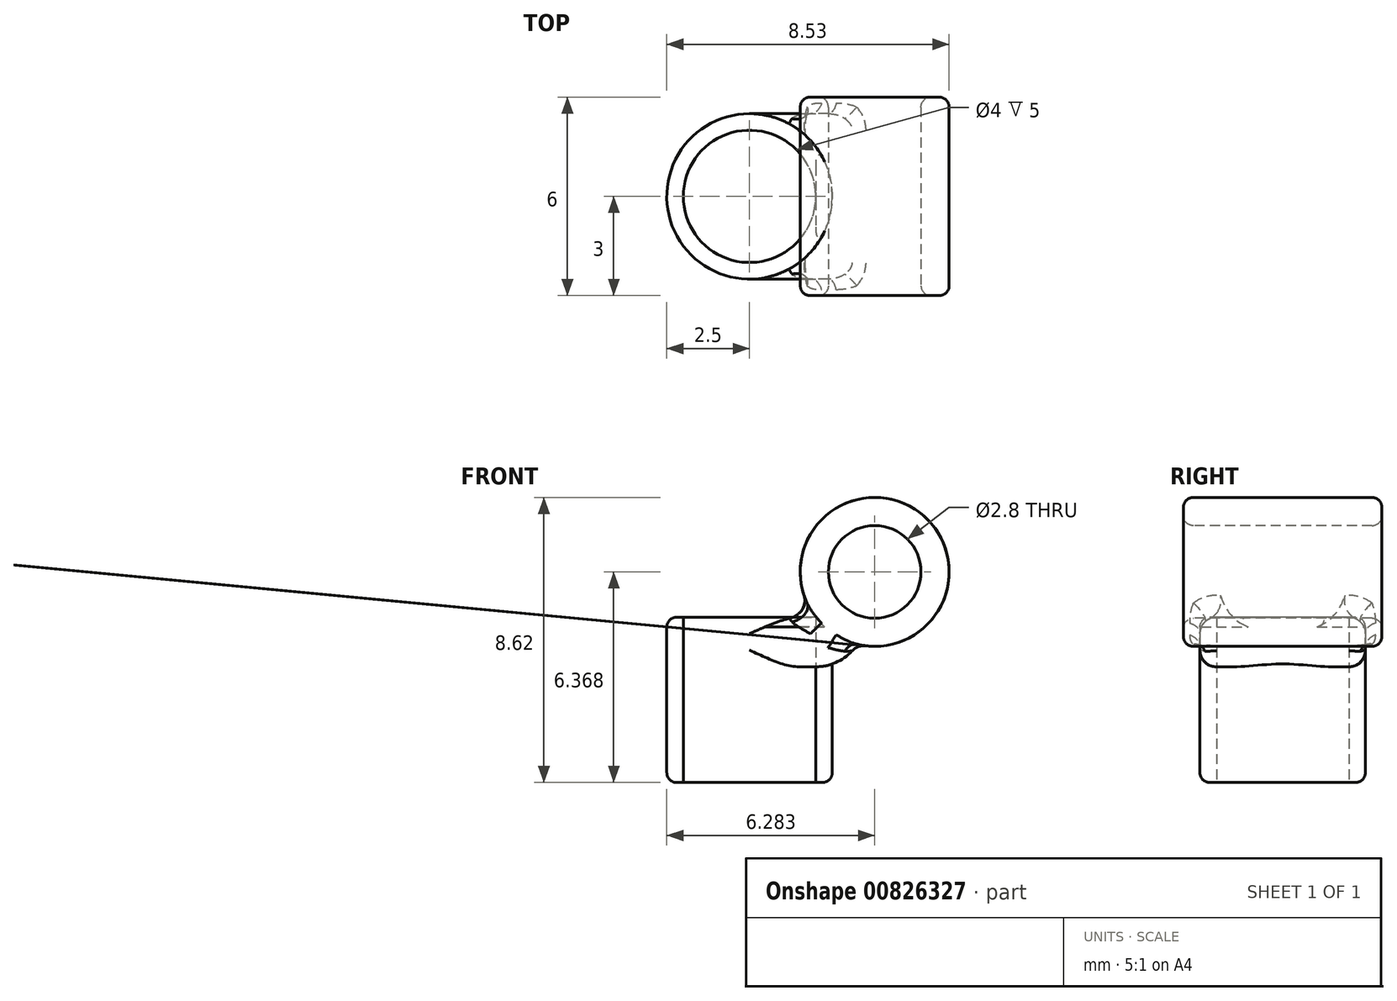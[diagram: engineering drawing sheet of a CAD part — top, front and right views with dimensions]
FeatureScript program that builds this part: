
annotation { "Feature Type Name" : "Feature", "Feature Type Description" : "" }
export const myFeature = defineFeature(function(context is Context, id is Id, definition is map)
    precondition{}
    {
        {
            var Q0;
            Q0=qCreatedBy(makeId("Top.planeOp"),FACE);
            var sketch = newSketch(context, id + "F0", { "sketchPlane" : qUnion([Q0])});
            skCircle(sketch, "E0", {"center": v(0, 0) * mm, "radius": 2 * mm});
            skCircle(sketch, "E1", {"center": v(0, 0) * mm, "radius": 2.5 * mm});
            skSolve(sketch);
        }
        {
            var Q0;
            Q0 = qSketchRegion(id + "F0", true);
            extrude(context, id + "F1", {"entities" : qUnion([Q0]), "depth" : 5 * mm, "offsetDistance" : 25 * mm});
        }
        {
            var Q0;
            Q0=qCreatedBy(makeId("Front.planeOp"),FACE);
            cPlane(context, id + "F2", {"entities" : qUnion([Q0]), "cplaneType" : CPlaneType.OFFSET, "offset" : 3 * mm, "width" : 150 * mm, "height" : 150 * mm});
        }
        {
            var Q0;
            Q0=qCreatedBy(id+"F2.planeOp",FACE);
            var sketch = newSketch(context, id + "F3", { "sketchPlane" : qUnion([Q0])});
            skCircle(sketch, "E2", {"center": v(3.78, 6.37) * mm, "radius": 2.25 * mm});
            skPoint(sketch, "E3.start.orphan", {"position": v(5, 0) * mm});
            skCircle(sketch, "E4", {"center": v(3.78, 6.37) * mm, "radius": 1.4 * mm});
            skSolve(sketch);
        }
        {
            var Q0;
            Q0 = qSketchRegion(id + "F3", true);
            extrude(context, id + "F4", {"entities" : qUnion([Q0]), "oppositeDirection" : true, "depth" : 6 * mm, "offsetDistance" : 25 * mm});
        }
        {
            var Q0;
            Q0=qCreatedBy(makeId("Top.planeOp"),FACE);
            cPlane(context, id + "F5", {"entities" : qUnion([Q0]), "cplaneType" : CPlaneType.OFFSET, "offset" : 3.5 * mm, "width" : 150 * mm, "height" : 150 * mm});
        }
        {
            var Q0;
            Q0=qCreatedBy(id+"F5.planeOp",FACE);
            var sketch = newSketch(context, id + "F6", { "sketchPlane" : qUnion([Q0])});
            skArc(sketch, "E5.0", {"start": v(0, -2.5) * mm, "mid": v(2.5, 0) * mm, "end": v(0, 2.5) * mm});
            skLineSegment(sketch, "E6", {"start": v(0, 2.5) * mm, "end": v(3.5, 2.5) * mm});
            skLineSegment(sketch, "E7", {"start": v(0, -2.5) * mm, "end": v(3.5, -2.5) * mm});
            skLineSegment(sketch, "E8", {"start": v(3.5, -2.5) * mm, "end": v(3.5, 2.5) * mm});
            skPoint(sketch, "E9.start.orphan", {"position": v(0, -0.17) * mm});
            skPoint(sketch, "E10.bottom.start.orphan", {"position": v(0, 78.67) * mm});
            skSolve(sketch);
        }
        {
            var Q0;
            Q0 = qSketchRegion(id + "F6", true);
            extrude(context, id + "F7", {"entities" : qUnion([Q0]), "depth" : 1.5 * mm, "offsetDistance" : 25 * mm});
        }
        {
            var Q0;
            Q0=makeQuery(id+"F7.opExtrude","CAP_EDGE",EDGE,{"disambiguationData":[OSD([sQuery(id+"F6.wireOp",EDGE,"E8")])],"isStart":true});
            fillet(context, id + "F8", {"entities" : qUnion([Q0]), "radius" : 1.5 * mm, "tangentPropagation" : true, "allowEdgeOverflow" : false});
        }
        {
            var Q0;
            Q0=makeQuery(id+"F7.opExtrude","CAP_EDGE",EDGE,{"disambiguationData":[OSD([sQuery(id+"F6.wireOp",EDGE,"E7")])],"isStart":true});
            var Q1;
            Q1=makeQuery(id+"F7.opExtrude","CAP_EDGE",EDGE,{"disambiguationData":[OSD([sQuery(id+"F6.wireOp",EDGE,"E7")])],"isStart":false});
            var Q2;
            Q2=makeQuery(id+"F7.opExtrude","CAP_EDGE",EDGE,{"disambiguationData":[OSD([sQuery(id+"F6.wireOp",EDGE,"E6")])],"isStart":true});
            var Q3;
            Q3=makeQuery(id+"F7.opExtrude","CAP_EDGE",EDGE,{"disambiguationData":[OSD([sQuery(id+"F6.wireOp",EDGE,"E6")])],"isStart":false});
            var Q4;
            {var subQ0=sQuery(id+"F6.wireOp",EDGE,"E8");Q4=makeQuery(id+"F8.opFillet","BLEND_EDGE",EDGE,{"blendedFrom":[makeQuery(id+"F7.opExtrude","CAP_EDGE",EDGE,{"disambiguationData":[OSD([subQ0])],"isStart":true}),makeQuery(id+"F7.opExtrude","CAP_FACE",FACE,{"disambiguationData":[OSD([sQuery(id+"F6.wireOp",EDGE,"E5.0"),sQuery(id+"F6.wireOp",EDGE,"E6"),sQuery(id+"F6.wireOp",EDGE,"E7"),subQ0])],"isStart":false})],"blendedInto":[makeQuery(id+"F7.opExtrude","CAP_FACE",FACE,{"disambiguationData":[OSD([sQuery(id+"F6.wireOp",EDGE,"E5.0"),sQuery(id+"F6.wireOp",EDGE,"E6"),sQuery(id+"F6.wireOp",EDGE,"E7"),subQ0])],"isStart":false})]});}
            fillet(context, id + "F9", {"entities" : qUnion([Q0, Q1, Q2, Q3, Q4]), "radius" : 0.5 * mm, "tangentPropagation" : true, "allowEdgeOverflow" : false});
        }
        {
            var Q0;
            Q0=makeQuery(id+"F4.opExtrude","CAP_FACE",FACE,{"disambiguationData":[OSD([sQuery(id+"F3.wireOp",EDGE,"E2"),sQuery(id+"F3.wireOp",EDGE,"E4")])],"isStart":true});
            var Q1;
            Q1=makeQuery(id+"F4.opExtrude","CAP_EDGE",EDGE,{"disambiguationData":[OSD([sQuery(id+"F3.wireOp",EDGE,"E4")])],"isStart":false});
            var Q2;
            Q2=makeQuery(id+"F4.opExtrude","CAP_FACE",FACE,{"disambiguationData":[OSD([sQuery(id+"F3.wireOp",EDGE,"E2"),sQuery(id+"F3.wireOp",EDGE,"E4")])],"isStart":false});
            var Q3;
            Q3=makeQuery(id+"F1.opExtrude","CAP_EDGE",EDGE,{"disambiguationData":[OSD([sQuery(id+"F0.wireOp",EDGE,"E1")])],"isStart":false});
            var Q4;
            Q4=makeQuery(id+"F1.opExtrude","CAP_EDGE",EDGE,{"disambiguationData":[OSD([sQuery(id+"F0.wireOp",EDGE,"E1")])],"isStart":true});
            fillet(context, id + "F10", {"entities" : qUnion([Q0, Q1, Q2, Q3, Q4]), "radius" : 0.3 * mm, "tangentPropagation" : true, "allowEdgeOverflow" : false});
        }
        {
            var Q0;
            Q0=makeQuery(id+"F1.opExtrude","SWEPT_BODY",BODY,{"disambiguationData":[OSD([sQuery(id+"F0.wireOp",EDGE,"E0"),sQuery(id+"F0.wireOp",EDGE,"E1")])]});
            var Q1;
            Q1=makeQuery(id+"F4.opExtrude","SWEPT_BODY",BODY,{"disambiguationData":[OSD([sQuery(id+"F3.wireOp",EDGE,"E2"),sQuery(id+"F3.wireOp",EDGE,"E4")])]});
            var Q2;
            Q2=makeQuery(id+"F7.opExtrude","SWEPT_BODY",BODY,{"disambiguationData":[OSD([sQuery(id+"F6.wireOp",EDGE,"E5.0"),sQuery(id+"F6.wireOp",EDGE,"E6"),sQuery(id+"F6.wireOp",EDGE,"E7"),sQuery(id+"F6.wireOp",EDGE,"E8")])]});
            booleanBodies(context, id + "F11", {"operationType" : BooleanOperationType.UNION, "tools" : qUnion([Q0, Q1, Q2])});
        }
        {
            var Q0;
            Q0=makeQuery(id+"F11.opBoolean","INTERSECT",EDGE,{"derivedFrom":[makeQuery(id+"F8.opFillet","BLEND_FACE",FACE,{"disambiguationData":[OSD([sQuery(id+"F6.wireOp",EDGE,"E8")])]}),makeQuery(id+"F4.opExtrude","SWEPT_FACE",FACE,{"disambiguationData":[OSD([sQuery(id+"F3.wireOp",EDGE,"E2")])]})]});
            fillet(context, id + "F12", {"entities" : qUnion([Q0]), "radius" : 0.5 * mm, "tangentPropagation" : true, "allowEdgeOverflow" : false});
        }
    });
